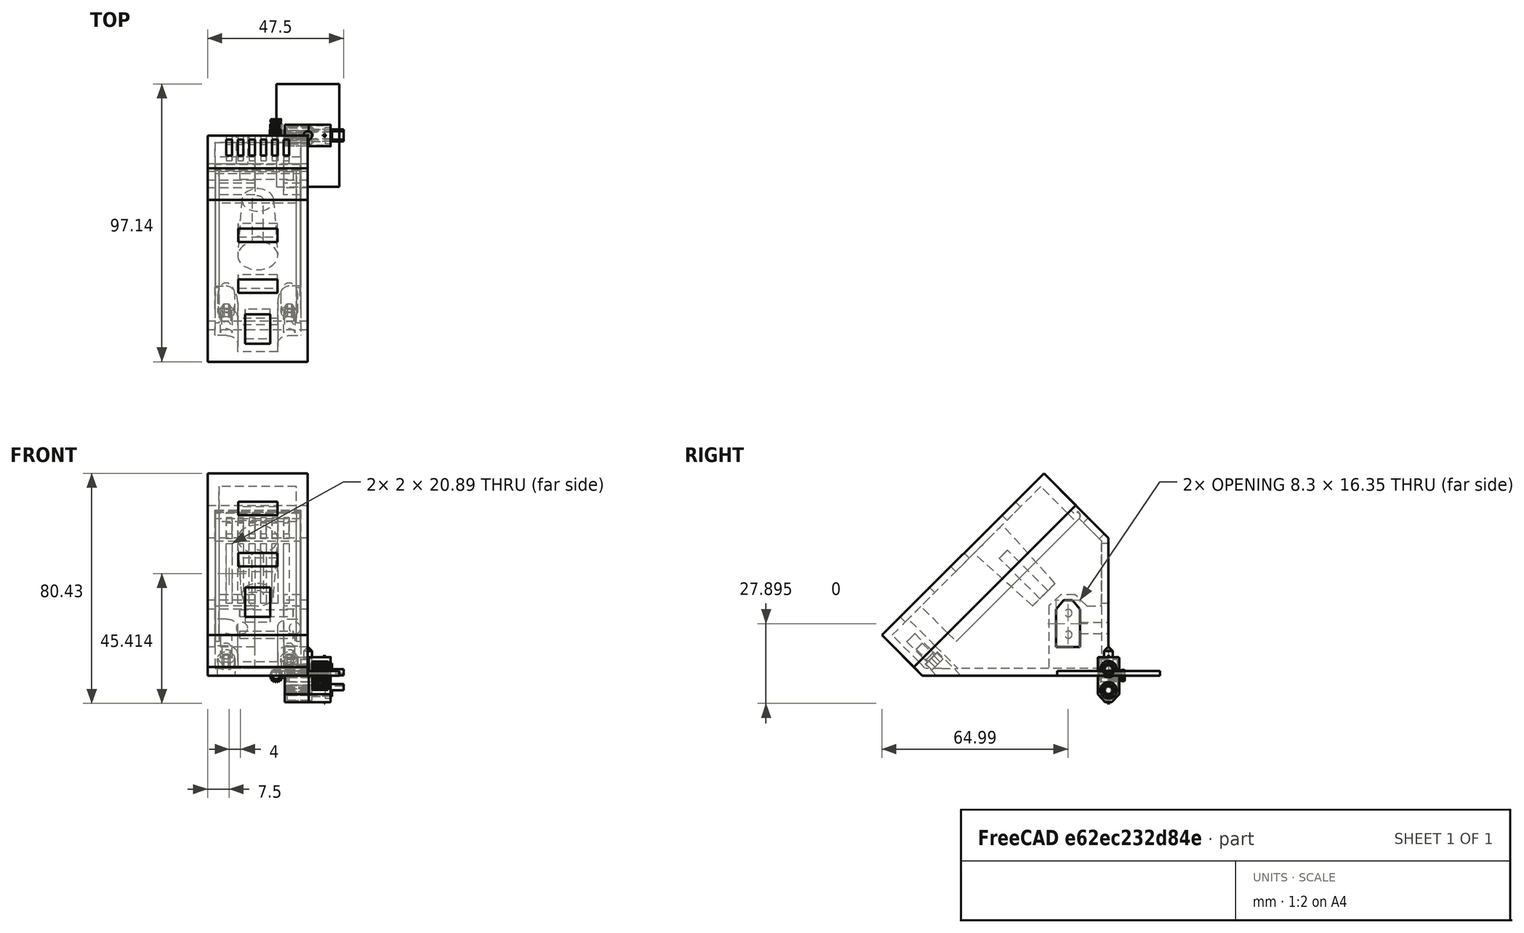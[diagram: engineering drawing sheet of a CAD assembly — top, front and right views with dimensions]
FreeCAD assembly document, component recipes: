
FREECAD ASSEMBLY — COMPONENT RECIPES ("moduleUSB_IP6505_QC2Sur_base35mm_012")

This assembly document has 12 components, labeled P0..P11 below (a component is one placed body or linked part). 10 of them carry a construction recipe — the FreeCAD feature program that regenerates the part from scratch, quoted from this document or its linked companion documents; the rest are supplied as boundary geometry only. No exploded tour is included for this assembly.
COMPONENT P0 — recipe-attached ("base", modeled in this document).
Construction recipe (the document's own serialized feature program — sketch geometry with constraints, then the solid features built on it; lengths are millimeters unless a unit is written):

FEATURE [PartDesign::FeatureBase] Clone
  BaseFeature = -> Slice_child0
FEATURE [PartDesign::Thickness] Thickness
  Base = -> Clone [Face7]
  BaseFeature = -> Clone
  Intersection = false
  Join = 0
  Mode = 0
  Reversed = true
  SupportTransform = false
  Value = 2.5
  expr: Value = <<sp>>.epaisseurParois
FEATURE [PartDesign::Plane] DatumPlane001  label="planXt"
  AttachmentOffset = pos=(0,0,-2.5) rot=(0,0,1;0rad)
  Length = 110.737
  MapMode = 5
  Placement = pos=(-2.5,6e-16,-6e-16) rot=(0.57735,0.57735,0.57735;2.0944rad)
  ResizeMode = 0
  Support = -> [YZ_Plane002]
  Width = 102.305
  expr: .AttachmentOffset.Base.z = -<<sp>>.epaisseurParois
FEATURE [Sketcher::SketchObject] Sketch002  label="sk_renfortXt"
  FullyConstrained = true
  MapMode = 5
  Placement = pos=(-2.5,6e-16,-6e-16) rot=(0.57735,0.57735,0.57735;2.0944rad)
  Support = -> [DatumPlane001]
  expr: .Constraints.dist = <<sp>>.xt60distanceAngleBord
  expr: .Constraints.epRf = <<sp>>.xt60epRenfort
  expr: Constraints[13] = <<sp>>.xt60largeurFetiere
  expr: Constraints[14] = <<sp>>.xt60hauteur
  expr: Constraints[15] = <<sp>>.xt60hauteurToit
  expr: Constraints[16] = <<sp>>.xt60base
  expr: Constraints[18] = .Constraints.dist
  expr: Constraints[31] = <<sp>>.epaisseurParois
  expr: Constraints[32] = .Constraints.epRf
  expr: Constraints[34] = .Constraints.epRf
  expr: Constraints[45] = <<sp>>.epaisseurParois
  sketch-geometry (17):
    g0: LineSegment StartX=-18.3 StartY=10 StartZ=0 EndX=-18.3 EndY=23.25 EndZ=0
    g1: LineSegment StartX=-18.3 StartY=23.25 StartZ=0 EndX=-15.65 EndY=25.75 EndZ=0
    g2: LineSegment StartX=-15.65 StartY=25.75 StartZ=0 EndX=-12.65 EndY=25.75 EndZ=0
    g3: LineSegment StartX=-12.65 StartY=25.75 StartZ=0 EndX=-10 EndY=23.25 EndZ=0
    g4: LineSegment StartX=-10 StartY=23.25 StartZ=0 EndX=-10 EndY=10 EndZ=0
    g5: LineSegment StartX=-10 StartY=10 StartZ=0 EndX=-18.3 EndY=10 EndZ=0
    g6: LineSegment StartX=-14.15 StartY=10 StartZ=0 EndX=-14.15 EndY=25.75 EndZ=0
    g7: LineSegment StartX=-16.6431 StartY=28.25 StartZ=0 EndX=-20.8 EndY=24.3284 EndZ=0
    g8: LineSegment StartX=-20.8 StartY=24.3284 StartZ=0 EndX=-20.8 EndY=2.5 EndZ=0
    g9: LineSegment StartX=-20.8 StartY=2.5 StartZ=0 EndX=-7.5 EndY=2.5 EndZ=0
    g10: LineSegment StartX=-7.5 StartY=2.5 StartZ=0 EndX=-7.5 EndY=24.3284 EndZ=0
    g11: LineSegment StartX=-7.5 StartY=24.3284 StartZ=0 EndX=-11.6569 EndY=28.25 EndZ=0
    g12: LineSegment StartX=-11.6569 StartY=28.25 StartZ=0 EndX=-16.6431 EndY=28.25 EndZ=0
    g13: LineSegment StartX=-7.5 StartY=24.3284 StartZ=0 EndX=-2.5 EndY=24.3284 EndZ=0
    g14: LineSegment StartX=-2.5 StartY=24.3284 StartZ=0 EndX=-2.5 EndY=2.5 EndZ=0
    g15: LineSegment StartX=-2.5 StartY=2.5 StartZ=0 EndX=-7.5 EndY=2.5 EndZ=0
    g16: LineSegment StartX=-7.5 StartY=2.5 StartZ=0 EndX=-7.5 EndY=24.3284 EndZ=0
  constraints (46):
    c: Vertical(g0)
    c: Coincident(g0,g1)
    c: Coincident(g1,g2)
    c: Horizontal(g2)
    c: Coincident(g2,g3)
    c: Coincident(g3,g4)
    c: Vertical(g4)
    c: Coincident(g4,g5)
    c: Coincident(g5,g0)
    c: Horizontal(g5)
    c: Symmetric(g1,g2,g6)
    c: Equal(g0,g4)
    c: Symmetric(g0,g4,g6)
    c: DistanceX(g2,g2) = 3
    c: DistanceY(g4,g4) = 13.25
    c: DistanceY(g3,g2) = 2.5
    c: DistanceX(g5,g5) = 8.3
    c: DistanceX(g4,g-1) = 10  'dist'
    c: DistanceY(g-1,g4) = 10
    c: Coincident(g7,g8)
    c: Vertical(g8)
    c: Coincident(g8,g9)
    c: Horizontal(g9)
    c: Coincident(g9,g10)
    c: Coincident(g10,g11)
    c: Coincident(g11,g12)
    c: Coincident(g12,g7)
    c: Symmetric(g7,g10,g6)
    c: Symmetric(g7,g11,g6)
    c: Symmetric(g8,g9,g6)
    c: DistanceX(g8,g0) = 2.5  'epRf'
    c: DistanceY(g-1,g9) = 2.5
    c: Distance(g7,g1) = 2.5
    c: Parallel(g1,g7)
    c: DistanceY(g2,g11) = 2.5
    c: Coincident(g13,g14)
    c: Coincident(g14,g15)
    c: Coincident(g15,g16)
    c: Coincident(g16,g13)
    c: Horizontal(g13)
    c: Horizontal(g15)
    c: Vertical(g14)
    c: Vertical(g16)
    c: Coincident(g13,g11)
    c: Horizontal(g14,g9)
    c: DistanceX(g14,g-1) = 2.5
FEATURE [PartDesign::Pad] Pad001  label="renfortXt"
  AllowMultiFace = false
  BaseFeature = -> Thickness
  Direction = (1,-1e-16,1e-16)
  Length = 30
  Length2 = 100
  Profile = -> Sketch002
  Reversed = true
  Type = 0
  expr: Length = <<sp>>.largeurModuleBase - 2 * <<sp>>.epaisseurParois
FEATURE [Sketcher::SketchObject] Sketch003  label="sk_trouXt"
  FullyConstrained = true
  MapMode = 5
  Placement = pos=(0,0,0) rot=(0.57735,0.57735,0.57735;2.0944rad)
  Support = -> [YZ_Plane002]
  expr: .Constraints.dist = <<sp>>.xt60distanceAngleBord
  expr: Constraints[13] = <<sp>>.xt60base
  expr: Constraints[14] = <<sp>>.xt60hauteur
  expr: Constraints[15] = <<sp>>.xt60hauteurToit + <<sp>>.xtJeu
  expr: Constraints[16] = <<sp>>.xt60largeurFetiere
  expr: Constraints[18] = .Constraints.dist
  sketch-geometry (7):
    g0: LineSegment StartX=-18.3 StartY=10 StartZ=0 EndX=-18.3 EndY=23.25 EndZ=0
    g1: LineSegment StartX=-18.3 StartY=23.25 StartZ=0 EndX=-15.65 EndY=26.35 EndZ=0
    g2: LineSegment StartX=-15.65 StartY=26.35 StartZ=0 EndX=-12.65 EndY=26.35 EndZ=0
    g3: LineSegment StartX=-12.65 StartY=26.35 StartZ=0 EndX=-10 EndY=23.25 EndZ=0
    g4: LineSegment StartX=-10 StartY=23.25 StartZ=0 EndX=-10 EndY=10 EndZ=0
    g5: LineSegment StartX=-10 StartY=10 StartZ=0 EndX=-18.3 EndY=10 EndZ=0
    g6: LineSegment StartX=-14.15 StartY=10 StartZ=0 EndX=-14.15 EndY=26.35 EndZ=0
  constraints (19):
    c: Vertical(g0)
    c: Coincident(g0,g1)
    c: Coincident(g1,g2)
    c: Horizontal(g2)
    c: Coincident(g2,g3)
    c: Coincident(g3,g4)
    c: Coincident(g4,g5)
    c: Coincident(g5,g0)
    c: Horizontal(g5)
    c: Symmetric(g1,g2,g6)
    c: Symmetric(g0,g3,g6)
    c: Vertical(g6)
    c: Symmetric(g0,g4,g6)
    c: DistanceX(g5,g5) = 8.3
    c: DistanceY(g4,g4) = 13.25
    c: DistanceY(g3,g2) = 3.1
    c: DistanceX(g2,g2) = 3
    c: DistanceX(g4,g-1) = 10  'dist'
    c: DistanceY(g-1,g4) = 10
FEATURE [PartDesign::Pocket] Pocket
  AllowMultiFace = false
  BaseFeature = -> Pad001
  Direction = (-1,2e-16,-3e-16)
  Length = 35
  Length2 = 100
  Profile = -> Sketch003
  Type = 0
  expr: Length = <<sp>>.largeurModuleBase
FEATURE [PartDesign::Plane] DatumPlane002  label="planDecoupeRenfortXt"
  AttachmentOffset = pos=(0,0,2.5) rot=(0,0,1;0rad)
  Length = 74.2466
  MapMode = 5
  Placement = pos=(0,-2.5,-6e-16) rot=(1,0,0;1.5708rad)
  ResizeMode = 0
  Support = -> [XZ_Plane002]
  Width = 98.8151
  expr: .AttachmentOffset.Base.z = <<sp>>.epaisseurParois
FEATURE [Sketcher::SketchObject] Sketch004  label="sk_decoupRenfXt"
  FullyConstrained = true
  MapMode = 5
  Placement = pos=(0,-2.5,-6e-16) rot=(1,0,0;1.5708rad)
  Support = -> [DatumPlane002]
  expr: Constraints[10] = <<sp>>.xt60LongueurRenfortPetit + <<sp>>.epaisseurParois
  expr: Constraints[11] = <<sp>>.largeurModuleBase - (<<sp>>.xt60longueurRenfortGrand + <<sp>>.epaisseurParois)
  expr: Constraints[8] = <<sp>>.epaisseurParois
  expr: Constraints[9] = <<sp>>.xt60distanceAngleBord + <<sp>>.xt60hauteur + <<sp>>.xt60hauteurToit + <<sp>>.xt60epRenfort
  sketch-geometry (4):
    g0: LineSegment StartX=-18.5 StartY=28.25 StartZ=0 EndX=-8.5 EndY=28.25 EndZ=0
    g1: LineSegment StartX=-8.5 StartY=28.25 StartZ=0 EndX=-8.5 EndY=2.5 EndZ=0
    g2: LineSegment StartX=-8.5 StartY=2.5 StartZ=0 EndX=-18.5 EndY=2.5 EndZ=0
    g3: LineSegment StartX=-18.5 StartY=2.5 StartZ=0 EndX=-18.5 EndY=28.25 EndZ=0
  constraints (12):
    c: Coincident(g0,g1)
    c: Coincident(g1,g2)
    c: Coincident(g2,g3)
    c: Coincident(g3,g0)
    c: Horizontal(g0)
    c: Horizontal(g2)
    c: Vertical(g1)
    c: Vertical(g3)
    c: DistanceY(g-1,g1) = 2.5
    c: DistanceY(g-1,g0) = 28.25
    c: DistanceX(g1,g-1) = 8.5
    c: DistanceX(g2,g-1) = 18.5
FEATURE [PartDesign::Pocket] Pocket001  label="decoupeRenfXt"
  AllowMultiFace = false
  BaseFeature = -> Pocket
  Direction = (0,1,2e-16)
  Length = 23.3
  Length2 = 100
  Profile = -> Sketch004
  Reversed = true
  Type = 0
  expr: Length = <<sp>>.xt60distanceAngleBord + <<sp>>.xt60base + 2 * <<sp>>.xt60epRenfort
FEATURE [Sketcher::SketchObject] Sketch005  label="xt60PercagePostMale"
  FullyConstrained = true
  MapMode = 5
  Placement = pos=(0,0,0) rot=(1,0,0;1.5708rad)
  Support = -> [XZ_Plane002]
  expr: Constraints[0] = <<sp>>.insertDiamPercage
  expr: Constraints[1] = <<sp>>.insertDistanceTrouBordMale
  expr: Constraints[2] = <<sp>>.insertHauteur
  sketch-geometry (1):
    g0: Circle CenterX=-4.5 CenterY=16.625 CenterZ=0 NormalX=0 NormalY=0 NormalZ=1 AngleXU=0 Radius=2
  constraints (3):
    c: Diameter(g0) = 4
    c: DistanceX(g0,g-1) = 4.5
    c: DistanceY(g-1,g0) = 16.625
FEATURE [PartDesign::Pocket] Pocket002  label="insertXtMale"
  AllowMultiFace = false
  BaseFeature = -> Pocket001
  Direction = (0,1,2e-16)
  Length = 10
  Length2 = 100
  Profile = -> Sketch005
  Reversed = true
  Type = 0
  expr: Length = <<sp>>.insertProfondeurPercage
FEATURE [Sketcher::SketchObject] Sketch006  label="xt60PercagePostFem"
  FullyConstrained = true
  MapMode = 5
  Placement = pos=(0,0,0) rot=(1,0,0;1.5708rad)
  Support = -> [XZ_Plane002]
  expr: Constraints[0] = <<sp>>.insertDiamPercage
  expr: Constraints[1] = <<sp>>.insertDistanceTrouBordFem
  expr: Constraints[2] = <<sp>>.insertHauteur
  sketch-geometry (1):
    g0: Circle CenterX=-23 CenterY=16.625 CenterZ=0 NormalX=0 NormalY=0 NormalZ=1 AngleXU=0 Radius=2
  constraints (3):
    c: Diameter(g0) = 4
    c: DistanceX(g0,g-1) = 23
    c: DistanceY(g-1,g0) = 16.625
FEATURE [PartDesign::Pocket] Pocket003  label="insertXt60Fem"
  AllowMultiFace = false
  BaseFeature = -> Pocket002
  Direction = (0,1,2e-16)
  Length = 10
  Length2 = 100
  Profile = -> Sketch006
  Reversed = true
  Type = 0
  expr: Length = <<sp>>.insertProfondeurPercage
FEATURE [PartDesign::Plane] DatumPlane003
  AttachmentOffset = pos=(0,0,2.5) rot=(0,0,1;0rad)
  Length = 74.9399
  MapMode = 2
  Placement = pos=(0,0,2.5) rot=(0,0,1;0rad)
  ResizeMode = 0
  Support = -> [XY_Plane002]
  Width = 107.94
  expr: .AttachmentOffset.Base.z = <<sp>>.epaisseurParois
FEATURE [PartDesign::Plane] DatumPlane004  label="planTrancheur"
  AttachmentOffset = pos=(0,0,71) rot=(-1,0,0;0.785398rad)
  Length = 77.3593
  MapMode = 5
  Placement = pos=(0,-71,-1.58e-14) rot=(1,0,0;0.785398rad)
  ResizeMode = 0
  Support = -> [XZ_Plane002]
  Width = 142.919
  expr: .AttachmentOffset.Base.z = <<sp>>.planTrancheur
FEATURE [Sketcher::SketchObject] Sketch008
  FullyConstrained = true
  MapMode = 5
  Placement = pos=(0,-71,-2.13e-14) rot=(1,0,0;0.785398rad)
  Support = -> [DatumPlane004]
  expr: .Constraints.dist = <<sp>>.epaisseurParois
  expr: Constraints[13] = <<sp>>.epaisseurParois
  expr: Constraints[16] = <<sp>>.insertDiamPercage / 2 + <<sp>>.insertFAVMargeDist
  expr: Constraints[1] = <<sp>>.insertFavDistAuZeroDuPLan
  expr: Constraints[21] = <<sp>>.insertFAVDistBord
  expr: Constraints[22] = <<sp>>.largeurModuleBase - <<sp>>.epaisseurParois
  sketch-geometry (7):
    g0: LineSegment StartX=-2.5 StartY=4.24264 StartZ=0 EndX=-32.5 EndY=4.24264 EndZ=0
    g1: LineSegment StartX=-6.5 StartY=14.7426 StartZ=0 EndX=-2.5 EndY=14.7426 EndZ=0
    g2: LineSegment StartX=-2.5 StartY=14.7426 StartZ=0 EndX=-2.5 EndY=6.74264 EndZ=0
    g3: LineSegment StartX=-2.5 StartY=6.74264 StartZ=0 EndX=-10.5 EndY=6.74264 EndZ=0
    g4: LineSegment StartX=-10.5 StartY=6.74264 StartZ=0 EndX=-10.5 EndY=10.7426 EndZ=0
    g5: ArcOfCircle CenterX=-6.5 CenterY=10.7426 CenterZ=0 NormalX=0 NormalY=0 NormalZ=1 AngleXU=0 Radius=4 StartAngle=1.5708 EndAngle=3.14159
    g6: LineSegment StartX=-6.5 StartY=10.7426 StartZ=0 EndX=-6.5 EndY=6.74264 EndZ=0
  constraints (23):
    c: Horizontal(g0)
    c: DistanceY(g-1,g0) = 4.24264
    c: DistanceX(g0,g-1) = 2.5  'dist'
    c: Horizontal(g1)
    c: Coincident(g1,g2)
    c: Vertical(g2)
    c: Coincident(g2,g3)
    c: Horizontal(g3)
    c: Coincident(g3,g4)
    c: Vertical(g4)
    c: Vertical(g2,g0)
    c: Equal(g3,g2)
    c: Equal(g4,g1)
    c: DistanceY(g0,g2) = 2.5
    c: Coincident(g5,g4)
    c: Coincident(g5,g1)
    c: DistanceX(g5,g2) = 4
    c: Coincident(g6,g5)
    c: PointOnObject(g6,g3)
    c: Vertical(g6)
    c: Vertical(g5,g1)
    c: DistanceX(g3,g3) = 8
    c: DistanceX(g0,g-1) = 32.5
FEATURE [PartDesign::Pad] Pad003  label="padTrouFAVDroite"
  AllowMultiFace = false
  BaseFeature = -> Pocket003
  Direction = (0,-0.707107,0.707107)
  Length = 10
  Length2 = 100
  Profile = -> Sketch008
  Reversed = true
  Type = 3
  UpToFace = -> DatumPlane003
FEATURE [Sketcher::SketchObject] Sketch009
  FullyConstrained = true
  MapMode = 5
  Placement = pos=(0,-71,-2.13e-14) rot=(1,0,0;0.785398rad)
  Support = -> [DatumPlane004]
  expr: .Constraints.larg = <<sp>>.insertFAVDistBord
  expr: Constraints[11] = .Constraints.larg / 2
  expr: Constraints[12] = <<sp>>.largeurModuleBase
  expr: Constraints[13] = <<sp>>.insertFavDistAuZeroDuPLan
  expr: Constraints[14] = <<sp>>.epaisseurParois
  expr: Constraints[15] = <<sp>>.epaisseurParois
  expr: Constraints[8] = .Constraints.larg
  sketch-geometry (6):
    g0: LineSegment StartX=-32.5 StartY=6.74264 StartZ=0 EndX=-24.5 EndY=6.74264 EndZ=0
    g1: LineSegment StartX=-24.5 StartY=6.74264 StartZ=0 EndX=-24.5 EndY=10.7426 EndZ=0
    g2: LineSegment StartX=-28.5 StartY=14.7426 StartZ=0 EndX=-32.5 EndY=14.7426 EndZ=0
    g3: LineSegment StartX=-32.5 StartY=14.7426 StartZ=0 EndX=-32.5 EndY=6.74264 EndZ=0
    g4: ArcOfCircle CenterX=-28.5 CenterY=10.7426 CenterZ=0 NormalX=0 NormalY=0 NormalZ=1 AngleXU=0 Radius=4 StartAngle=2e-16 EndAngle=1.5708
    g5: GeomPoint X=-35 Y=4.24264 Z=0
  constraints (16):
    c: Coincident(g0,g1)
    c: Coincident(g2,g3)
    c: Coincident(g3,g0)
    c: Horizontal(g0)
    c: Horizontal(g2)
    c: Vertical(g1)
    c: Vertical(g3)
    c: DistanceX(g0,g0) = 8  'larg'
    c: DistanceY(g3,g3) = 8
    c: Tangent(g2,g4) = -1.5708
    c: Tangent(g1,g4) = -1.5708
    c: DistanceX(g0,g4) = 4
    c: DistanceX(g5,g-1) = 35
    c: DistanceY(g-1,g5) = 4.24264
    c: DistanceX(g5,g0) = 2.5
    c: DistanceY(g5,g0) = 2.5
FEATURE [PartDesign::Pad] Pad004  label="padTrouFavGauche"
  AllowMultiFace = false
  BaseFeature = -> Pad003
  Direction = (0,-0.707107,0.707107)
  Length = 10
  Length2 = 100
  Profile = -> Sketch009
  Type = 3
  UpToFace = -> DatumPlane003 [Plane]
FEATURE [Sketcher::SketchObject] Sketch010
  FullyConstrained = true
  MapMode = 5
  Placement = pos=(0,-71,-2.13e-14) rot=(1,0,0;0.785398rad)
  Support = -> [DatumPlane004]
  expr: Constraints[0] = <<sp>>.insertFAVDistBord / 2 + <<sp>>.epaisseurParois
  expr: Constraints[1] = <<sp>>.insertFavDistAuZeroDuPLan + <<sp>>.epaisseurParois + <<sp>>.insertFAVDistBord / 2
  expr: Constraints[2] = <<sp>>.insertDiamPercage
  sketch-geometry (1):
    g0: Circle CenterX=-6.5 CenterY=10.7426 CenterZ=0 NormalX=0 NormalY=0 NormalZ=1 AngleXU=0 Radius=2
  constraints (3):
    c: DistanceX(g0,g-1) = 6.5
    c: DistanceY(g-1,g0) = 10.7426
    c: Diameter(g0) = 4
FEATURE [PartDesign::Pocket] Pocket004  label="trouDroit"
  AllowMultiFace = false
  BaseFeature = -> Pad004
  Direction = (0,0.707107,-0.707107)
  Length = 5
  Length2 = 100
  Profile = -> Sketch010
  Type = 1
FEATURE [Sketcher::SketchObject] Sketch011
  FullyConstrained = true
  MapMode = 5
  Placement = pos=(0,-71,-2.13e-14) rot=(1,0,0;0.785398rad)
  Support = -> [DatumPlane004]
  expr: Constraints[0] = <<sp>>.insertDiamPercage
  expr: Constraints[1] = <<sp>>.largeurModuleBase - <<sp>>.epaisseurParois - <<sp>>.insertFAVDistBord / 2
  expr: Constraints[2] = <<sp>>.insertFavDistAuZeroDuPLan + <<sp>>.epaisseurParois + <<sp>>.insertFAVDistBord / 2
  sketch-geometry (1):
    g0: Circle CenterX=-28.5 CenterY=10.7426 CenterZ=0 NormalX=0 NormalY=0 NormalZ=1 AngleXU=0 Radius=2
  constraints (3):
    c: Diameter(g0) = 4
    c: DistanceX(g0,g-1) = 28.5
    c: DistanceY(g-1,g0) = 10.7426
FEATURE [PartDesign::Pocket] Pocket005  label="trouGauche"
  AllowMultiFace = false
  BaseFeature = -> Pocket004
  Direction = (0,0.707107,-0.707107)
  Length = 5
  Length2 = 100
  Profile = -> Sketch011
  Type = 1
FEATURE [PartDesign::Plane] DatumPlane005  label="planTeteVisFav"
  AttachmentOffset = pos=(0,0,68) rot=(-1,0,0;0.785398rad)
  Length = 77.3593
  MapMode = 5
  Placement = pos=(0,-68,-1.51e-14) rot=(1,0,0;0.785398rad)
  ResizeMode = 0
  Support = -> [XZ_Plane002]
  Width = 142.919
  expr: .AttachmentOffset.Base.z = <<sp>>.planTrancheur - 3
FEATURE [Sketcher::SketchObject] Sketch012
  ExternalGeometry = -> [Pocket005]
  FullyConstrained = true
  MapMode = 5
  Placement = pos=(0,-68,-1.42e-14) rot=(1,0,0;0.785398rad)
  Support = -> [DatumPlane005]
  expr: Constraints[1] = <<sp>>.visM3DiamEncastrement
  sketch-geometry (2):
    g0: Circle CenterX=-6.5 CenterY=8.62132 CenterZ=0 NormalX=0 NormalY=0 NormalZ=1 AngleXU=0 Radius=3
    g1: Circle CenterX=-28.5 CenterY=8.62132 CenterZ=0 NormalX=0 NormalY=0 NormalZ=1 AngleXU=0 Radius=3
  constraints (4):
    c: Equal(g0,g1)
    c: Diameter(g1) = 6
    c: Coincident(g1,g-4)
    c: Coincident(g-3,g0)
FEATURE [PartDesign::Pocket] Pocket006  label="evidementTeteVisFav"
  AllowMultiFace = false
  BaseFeature = -> Pocket005
  Direction = (0,0.707107,-0.707107)
  Length = 20
  Length2 = 100
  Profile = -> Sketch012
  Type = 1
FEATURE [Sketcher::SketchObject] Sketch014
  FullyConstrained = true
  MapMode = 5
  Placement = pos=(0,0,0) rot=(1,0,0;1.5708rad)
  Support = -> [XZ_Plane002]
  expr: Constraints[12] = <<sp>>.xt60distanceAngleBord + <<sp>>.xt60hauteur + <<sp>>.ventilDistBordFente
  expr: Constraints[13] = <<sp>>.ventilLargeurFentes
  expr: Constraints[14] = <<sp>>.ventilEcartfente / 2
  expr: Constraints[15] = <<sp>>.hauteurDuDos - <<sp>>.ventilDistBordFente
  expr: Constraints[2] = <<sp>>.hauteurDuDos
  expr: Constraints[3] = <<sp>>.largeurModuleBase / 2
  sketch-geometry (5):
    g0: LineSegment StartX=-17.5 StartY=0 StartZ=0 EndX=-17.5 EndY=48.1371 EndZ=0
    g1: LineSegment StartX=-20.5 StartY=46.1371 StartZ=0 EndX=-18.5 EndY=46.1371 EndZ=0
    g2: LineSegment StartX=-18.5 StartY=46.1371 StartZ=0 EndX=-18.5 EndY=25.25 EndZ=0
    g3: LineSegment StartX=-18.5 StartY=25.25 StartZ=0 EndX=-20.5 EndY=25.25 EndZ=0
    g4: LineSegment StartX=-20.5 StartY=25.25 StartZ=0 EndX=-20.5 EndY=46.1371 EndZ=0
  constraints (16):
    c: PointOnObject(g0,g-1)
    c: Vertical(g0)
    c: DistanceY(g0,g0) = 48.1371
    c: DistanceX(g0,g-1) = 17.5
    c: Coincident(g1,g2)
    c: Coincident(g2,g3)
    c: Coincident(g3,g4)
    c: Coincident(g4,g1)
    c: Horizontal(g1)
    c: Horizontal(g3)
    c: Vertical(g2)
    c: Vertical(g4)
    c: DistanceY(g-1,g2) = 25.25
    c: DistanceX(g1,g1) = 2
    c: DistanceX(g2,g0) = 1
    c: DistanceY(g-1,g1) = 46.1371
FEATURE [PartDesign::Pocket] Pocket008  label="ventilFente1"
  AllowMultiFace = false
  BaseFeature = -> Pocket006
  Direction = (0,1,2e-16)
  Length = 2.5
  Length2 = 100
  Profile = -> Sketch014
  Reversed = true
  Type = 0
  expr: Length = <<sp>>.epaisseurParois
FEATURE [PartDesign::LinearPattern] LinearPattern  label="ventilDosRepeat1"
  BaseFeature = -> Pocket008
  Direction = -> Sketch014 [H_Axis]
  Length = 8
  Occurrences = 3
  Originals = -> [Pocket008]
  Reversed = true
  expr: Length = <<sp>>.ventilLargeurRepet
  expr: Occurrences = <<sp>>.ventilNbrFents
FEATURE [PartDesign::LinearPattern] LinearPattern001  label="ventilDosRepeat2"
  BaseFeature = -> LinearPattern
  Direction = -> Sketch014 [H_Axis]
  Length = 12
  Occurrences = 4
  Originals = -> [Pocket008]
  expr: Length = <<sp>>.ventilLargeurRepet + <<sp>>.ventilEcartfente + <<sp>>.ventilLargeurFentes
  expr: Occurrences = <<sp>>.ventilNbrFents + 1
FEATURE [PartDesign::Plane] DatumPlane006  label="planVentilSup"
  AttachmentOffset = pos=(0,0,-48.1371) rot=(1,0,0;0.785398rad)
  Length = 77.3593
  MapMode = 5
  Placement = pos=(0,48.1371,1.07e-14) rot=(1,0,0;2.35619rad)
  ResizeMode = 0
  Support = -> [XZ_Plane002]
  Width = 142.919
  expr: .AttachmentOffset.Base.z = -<<sp>>.hauteurDuDos
FEATURE [Sketcher::SketchObject] Sketch015
  FullyConstrained = true
  MapMode = 5
  Placement = pos=(0,48.1371,1.07e-14) rot=(1,0,0;2.35619rad)
  Support = -> [DatumPlane006]
  expr: Constraints[10] = <<sp>>.ventilLargeurFentes
  expr: Constraints[11] = (<<sp>>.largeurModuleBase + <<sp>>.ventilEcartfente) / 2
  expr: Constraints[8] = <<sp>>.distanceAuZeroPlanBorArriere + <<sp>>.ventilDistBordFente
  expr: Constraints[9] = <<sp>>.longPetitRetSupSansFav - 2 * <<sp>>.ventilDistBordFente - <<sp>>.favBordureProf
  sketch-geometry (4):
    g0: LineSegment StartX=-18.5 StartY=78.0926 StartZ=0 EndX=-20.5 EndY=78.0926 EndZ=0
    g1: LineSegment StartX=-20.5 StartY=78.0926 StartZ=0 EndX=-20.5 EndY=70.0761 EndZ=0
    g2: LineSegment StartX=-20.5 StartY=70.0761 StartZ=0 EndX=-18.5 EndY=70.0761 EndZ=0
    g3: LineSegment StartX=-18.5 StartY=70.0761 StartZ=0 EndX=-18.5 EndY=78.0926 EndZ=0
  constraints (12):
    c: Coincident(g0,g1)
    c: Coincident(g1,g2)
    c: Coincident(g2,g3)
    c: Coincident(g3,g0)
    c: Horizontal(g0)
    c: Horizontal(g2)
    c: Vertical(g1)
    c: Vertical(g3)
    c: DistanceY(g-1,g2) = 70.0761
    c: DistanceY(g2,g0) = 8.01652
    c: DistanceX(g0,g0) = 2
    c: DistanceX(g2,g-1) = 18.5
FEATURE [PartDesign::Pocket] Pocket009  label="ventilSupFente"
  AllowMultiFace = false
  BaseFeature = -> LinearPattern001
  Direction = (0,0.707107,0.707107)
  Length = 5
  Length2 = 100
  Profile = -> Sketch015
  Reversed = true
  Type = 0
FEATURE [PartDesign::LinearPattern] LinearPattern002  label="ventilSupRepeat1"
  BaseFeature = -> Pocket009
  Direction = -> Sketch015 [H_Axis]
  Length = 8
  Occurrences = 3
  Originals = -> [Pocket009]
  Reversed = true
  expr: Length = <<sp>>.ventilLargeurRepet
  expr: Occurrences = <<sp>>.ventilNbrFents
FEATURE [PartDesign::LinearPattern] LinearPattern003  label="ventilSupRepeat2"
  BaseFeature = -> LinearPattern002
  Direction = -> Sketch015 [H_Axis]
  Length = 12
  Occurrences = 4
  Originals = -> [Pocket009]
  expr: Length = <<sp>>.ventilLargeurRepet + <<sp>>.ventilEcartfente + <<sp>>.ventilLargeurFentes
  expr: Occurrences = <<sp>>.ventilNbrFents + 1
FEATURE [PartDesign::Body] Body001  label="base"
  BaseFeature = -> Slice_child0
  Group = -> [Clone,Thickness,DatumPlane001,Sketch002,Pad001,Sketch003,Pocket,DatumPlane002,Sketch004,Pocket001,Sketch005,Pocket002,Sketch006,Pocket003,DatumPlane003,DatumPlane004,Sketch008,Pad003,Sketch009,Pad004,Sketch010,Pocket004,Sketch011,Pocket005,DatumPlane005,Sketch012,Pocket006,Sketch014,Pocket008,LinearPattern,LinearPattern001,DatumPlane006,Sketch015,Pocket009,LinearPattern002,LinearPattern003,+3 more]
  Origin = -> Origin002
  Tip = -> Pocket015
COMPONENT P1 — recipe-attached ("faceAvant", modeled in this document).
Construction recipe (the document's own serialized feature program — sketch geometry with constraints, then the solid features built on it; lengths are millimeters unless a unit is written):

FEATURE [PartDesign::FeatureBase] Clone001
  BaseFeature = -> Slice_child1
FEATURE [PartDesign::Thickness] Thickness001
  Base = -> Clone001 [Face5]
  BaseFeature = -> Clone001
  Intersection = false
  Join = 0
  Mode = 0
  Reversed = true
  SupportTransform = false
  Value = 2.5
  expr: Value = <<sp>>.epaisseurParois
FEATURE [PartDesign::Plane] DatumPlane007  label="planTrancheurBis"
  AttachmentOffset = pos=(0,0,71) rot=(-1,0,0;0.785398rad)
  Length = 78.4163
  MapMode = 5
  Placement = pos=(0,-71,-1.58e-14) rot=(1,0,0;0.785398rad)
  ResizeMode = 0
  Support = -> [XZ_Plane003]
  Width = 159.734
  expr: .AttachmentOffset.Base.z = <<sp>>.planTrancheur
FEATURE [Sketcher::SketchObject] Sketch016  label="sk_insertFavDroit"
  FullyConstrained = true
  MapMode = 5
  Placement = pos=(0,-71,-2.13e-14) rot=(1,0,0;0.785398rad)
  Support = -> [DatumPlane007]
  expr: Constraints[11] = <<sp>>.insertFAVDistBord
  expr: Constraints[14] = <<sp>>.insertFAVDistBord / 2
  expr: Constraints[7] = <<sp>>.epaisseurParois
  expr: Constraints[8] = <<sp>>.insertFavDistAuZeroDuPLan + <<sp>>.epaisseurParois
  expr: Constraints[9] = <<sp>>.insertFAVDistBord
  sketch-geometry (5):
    g0: LineSegment StartX=-6.5 StartY=14.7426 StartZ=0 EndX=-2.5 EndY=14.7426 EndZ=0
    g1: LineSegment StartX=-2.5 StartY=14.7426 StartZ=0 EndX=-2.5 EndY=6.74264 EndZ=0
    g2: LineSegment StartX=-2.5 StartY=6.74264 StartZ=0 EndX=-10.5 EndY=6.74264 EndZ=0
    g3: LineSegment StartX=-10.5 StartY=6.74264 StartZ=0 EndX=-10.5 EndY=10.7426 EndZ=0
    g4: ArcOfCircle CenterX=-6.5 CenterY=10.7426 CenterZ=0 NormalX=0 NormalY=0 NormalZ=1 AngleXU=0 Radius=4 StartAngle=1.5708 EndAngle=3.14159
  constraints (15):
    c: Horizontal(g0)
    c: Coincident(g0,g1)
    c: Vertical(g1)
    c: Coincident(g1,g2)
    c: Horizontal(g2)
    c: Coincident(g2,g3)
    c: Vertical(g3)
    c: DistanceX(g1,g-1) = 2.5
    c: DistanceY(g-1,g1) = 6.74264
    c: DistanceY(g1,g1) = 8
    c: Equal(g3,g0)
    c: DistanceX(g2,g2) = 8
    c: Coincident(g4,g0)
    c: Tangent(g4,g3) = 1.5708
    c: DistanceX(g4,g1) = 4
FEATURE [PartDesign::Pad] Pad005  label="padInsertFavDroit"
  AllowMultiFace = false
  BaseFeature = -> Thickness001
  Direction = (0,-0.707107,0.707107)
  Length = 10
  Length2 = 100
  Profile = -> Sketch016
  Type = 2
FEATURE [Sketcher::SketchObject] Sketch017  label="sp_padInserFavGauch"
  FullyConstrained = true
  MapMode = 5
  Placement = pos=(0,-71,-2.13e-14) rot=(1,0,0;0.785398rad)
  Support = -> [DatumPlane007]
  expr: Constraints[10] = <<sp>>.insertFAVDistBord
  expr: Constraints[12] = <<sp>>.insertFAVDistBord / 2
  expr: Constraints[13] = <<sp>>.largeurModuleBase
  expr: Constraints[14] = <<sp>>.insertFavDistAuZeroDuPLan
  expr: Constraints[15] = <<sp>>.epaisseurParois
  expr: Constraints[16] = <<sp>>.epaisseurParois
  sketch-geometry (6):
    g0: LineSegment StartX=-28.5 StartY=14.7426 StartZ=0 EndX=-32.5 EndY=14.7426 EndZ=0
    g1: LineSegment StartX=-32.5 StartY=14.7426 StartZ=0 EndX=-32.5 EndY=6.74264 EndZ=0
    g2: LineSegment StartX=-32.5 StartY=6.74264 StartZ=0 EndX=-24.5 EndY=6.74264 EndZ=0
    g3: LineSegment StartX=-24.5 StartY=6.74264 StartZ=0 EndX=-24.5 EndY=10.7426 EndZ=0
    g4: ArcOfCircle CenterX=-28.5 CenterY=10.7426 CenterZ=0 NormalX=0 NormalY=0 NormalZ=1 AngleXU=0 Radius=4 StartAngle=-1.32614e-11 EndAngle=1.5708
    g5: GeomPoint X=-35 Y=4.24264 Z=0
  constraints (17):
    c: Horizontal(g0)
    c: Coincident(g0,g1)
    c: Vertical(g1)
    c: Coincident(g1,g2)
    c: Horizontal(g2)
    c: Coincident(g2,g3)
    c: Vertical(g3)
    c: Equal(g3,g0)
    c: Equal(g2,g1)
    c: Coincident(g0,g4)
    c: DistanceX(g2,g2) = 8
    c: Tangent(g4,g3) = -1.5708
    c: DistanceX(g0,g0) = 4
    c: DistanceX(g5,g-1) = 35
    c: DistanceY(g-1,g5) = 4.24264
    c: DistanceY(g5,g1) = 2.5
    c: DistanceX(g5,g1) = 2.5
FEATURE [PartDesign::Pad] Pad006  label="padInsertFavGauch"
  AllowMultiFace = false
  BaseFeature = -> Pad005
  Direction = (0,-0.707107,0.707107)
  Length = 10
  Length2 = 100
  Profile = -> Sketch017
  Type = 2
FEATURE [Sketcher::SketchObject] Sketch018  label="skPercageInsertFavDroit"
  FullyConstrained = true
  MapMode = 5
  Placement = pos=(0,-71,-2.13e-14) rot=(1,0,0;0.785398rad)
  Support = -> [DatumPlane007]
  expr: Constraints[0] = <<sp>>.insertDiamPercage
  expr: Constraints[1] = <<sp>>.insertFavDistAuZeroDuPLan + <<sp>>.epaisseurParois + <<sp>>.insertFAVDistBord / 2
  expr: Constraints[2] = <<sp>>.epaisseurParois + <<sp>>.insertFAVDistBord / 2
  expr: Constraints[7] = <<sp>>.largeurModuleBase - 2 * <<sp>>.epaisseurParois - <<sp>>.insertFAVDistBord
  sketch-geometry (3):
    g0: Circle CenterX=-6.5 CenterY=10.7426 CenterZ=0 NormalX=0 NormalY=0 NormalZ=1 AngleXU=0 Radius=2
    g1: Circle CenterX=-28.5 CenterY=10.7426 CenterZ=0 NormalX=0 NormalY=0 NormalZ=1 AngleXU=0 Radius=2
    g2: LineSegment StartX=-28.5 StartY=10.7426 StartZ=0 EndX=-6.5 EndY=10.7426 EndZ=0
  constraints (8):
    c: Diameter(g0) = 4
    c: DistanceY(g-1,g0) = 10.7426
    c: DistanceX(g0,g-1) = 6.5
    c: Equal(g0,g1)
    c: Coincident(g2,g1)
    c: Coincident(g2,g0)
    c: Horizontal(g2)
    c: DistanceX(g2,g2) = 22
FEATURE [PartDesign::Pocket] Pocket010  label="trouInsertFavDroit"
  AllowMultiFace = false
  BaseFeature = -> Pad006
  Direction = (0,0.707107,-0.707107)
  Length = 8
  Length2 = 100
  Profile = -> Sketch018
  Reversed = true
  Type = 0
  expr: Length = <<sp>>.insertFavProfondeur
FEATURE [PartDesign::Plane] DatumPlane011  label="planFaceAvant"
  AttachmentOffset = pos=(0,0,93.2843) rot=(-1,0,0;0.785398rad)
  Length = 78.4163
  MapMode = 5
  Placement = pos=(0,-93.2843,-2.07e-14) rot=(1,0,0;0.785398rad)
  ResizeMode = 0
  Support = -> [XZ_Plane003]
  Width = 159.734
  expr: .AttachmentOffset.Base.z = <<sp>>.planFaceAvant
FEATURE [Sketcher::SketchObject] Sketch030  label="sk_rebordFav"
  FullyConstrained = true
  MapMode = 5
  Placement = pos=(0,-71,-2.13e-14) rot=(1,0,0;0.785398rad)
  Support = -> [DatumPlane007]
  expr: Constraints[0] = <<sp>>.insertFavDistAuZeroDuPLan
  expr: Constraints[19] = <<sp>>.epaisseurParois
  expr: Constraints[20] = <<sp>>.favEpBordure
  expr: Constraints[21] = <<sp>>.favDistBordPlan
  expr: Constraints[22] = <<sp>>.largeurModuleBase - 2 * <<sp>>.epaisseurParois
  expr: Constraints[23] = <<sp>>.favEpBordure
  expr: Constraints[24] = <<sp>>.Face - <<sp>>.epaisseurParois
  expr: Constraints[25] = <<sp>>.favEpBordure
  sketch-geometry (9):
    g0: GeomPoint X=0 Y=4.24264 Z=0
    g1: LineSegment StartX=-32.5 StartY=20.9853 StartZ=0 EndX=-32.5 EndY=81.7426 EndZ=0
    g2: LineSegment StartX=-32.5 StartY=81.7426 StartZ=0 EndX=-2.5 EndY=81.7426 EndZ=0
    g3: LineSegment StartX=-2.5 StartY=81.7426 StartZ=0 EndX=-2.5 EndY=20.9853 EndZ=0
    g4: LineSegment StartX=-2.5 StartY=20.9853 StartZ=0 EndX=-4 EndY=20.9853 EndZ=0
    g5: LineSegment StartX=-4 StartY=20.9853 StartZ=0 EndX=-4 EndY=80.2426 EndZ=0
    g6: LineSegment StartX=-4 StartY=80.2426 StartZ=0 EndX=-31 EndY=80.2426 EndZ=0
    g7: LineSegment StartX=-31 StartY=80.2426 StartZ=0 EndX=-31 EndY=20.9853 EndZ=0
    g8: LineSegment StartX=-31 StartY=20.9853 StartZ=0 EndX=-32.5 EndY=20.9853 EndZ=0
  constraints (26):
    c: DistanceY(g-1,g0) = 4.24264
    c: Vertical(g0,g-1)
    c: Vertical(g1)
    c: Coincident(g1,g2)
    c: Horizontal(g2)
    c: Coincident(g2,g3)
    c: Vertical(g3)
    c: Coincident(g3,g4)
    c: Horizontal(g4)
    c: Coincident(g4,g5)
    c: Vertical(g5)
    c: Coincident(g5,g6)
    c: Horizontal(g6)
    c: Coincident(g6,g7)
    c: Vertical(g7)
    c: Coincident(g7,g8)
    c: Coincident(g8,g1)
    c: Horizontal(g8)
    c: Horizontal(g7,g4)
    c: DistanceX(g3,g0) = 2.5
    c: DistanceX(g4,g4) = 1.5
    c: DistanceY(g0,g3) = 16.7426
    c: DistanceX(g1,g3) = 30
    c: DistanceY(g5,g2) = 1.5
    c: DistanceY(g0,g2) = 77.5
    c: DistanceX(g1,g7) = 1.5
FEATURE [PartDesign::Pad] Pad014  label="favRebordSupport"
  AllowMultiFace = false
  BaseFeature = -> Pocket010
  Direction = (0,-0.707107,0.707107)
  Length = 10
  Length2 = 100
  Profile = -> Sketch030
  Type = 3
  UpToFace = -> Pocket010 [Face13]
FEATURE [PartDesign::Pad] Pad015  label="favRebord"
  AllowMultiFace = false
  BaseFeature = -> Pad014
  Direction = (0,-0.707107,0.707107)
  Length = 4.15
  Length2 = 100
  Profile = -> Sketch030
  Reversed = true
  Type = 0
  expr: Length = <<sp>>.favBordureProf
FEATURE [Sketcher::SketchObject] Sketch031  label="sk_bourlet"
  ExternalGeometry = -> [Pad015]
  FullyConstrained = true
  MapMode = 5
  Placement = pos=(-2.5,0,0) rot=(0.57735,0.57735,0.57735;2.0944rad)
  Support = -> [Pad015]
  expr: Constraints[3] = <<sp>>.bourletMaintientRayon - <<sp>>.bourletRayonJeu
  sketch-geometry (2):
    g0: ArcOfCircle CenterX=-11.184 CenterY=55.7855 CenterZ=0 NormalX=0 NormalY=0 NormalZ=1 AngleXU=0 Radius=1.3 StartAngle=5.49779 EndAngle=8.63938
    g1: LineSegment StartX=-12.1032 StartY=56.7048 StartZ=0 EndX=-10.2647 EndY=54.8663 EndZ=0
  constraints (6):
    c: Coincident(g0,g-3)
    c: PointOnObject(g0,g-3)
    c: PointOnObject(g0,g-3)
    c: Radius(g0) = 1.3
    c: Coincident(g1,g0)
    c: Coincident(g1,g0)
FEATURE [PartDesign::Pad] Pad016  label="bourlet"
  AllowMultiFace = false
  BaseFeature = -> Pad015
  Direction = (1,0,0)
  Length = 10
  Length2 = 100
  Profile = -> Sketch031
  Reversed = true
  Type = 3
  UpToFace = -> Pad015 [Face11]
FEATURE [Sketcher::SketchObject] Sketch039
  FullyConstrained = true
  MapMode = 5
  Placement = pos=(0,-71,-2.13e-14) rot=(1,0,0;0.785398rad)
  Support = -> [DatumPlane007]
  expr: Constraints[20] = <<sp>>.favBordureJeu / 2
  expr: Constraints[21] = <<sp>>.epaisseurParois
  expr: Constraints[22] = <<sp>>.largeurModuleBase - 2 * <<sp>>.epaisseurParois
  expr: Constraints[23] = <<sp>>.insertFavDistAuZeroDuPLan + <<sp>>.favDistBordPlan
  expr: Constraints[27] = <<sp>>.insertFavDistAuZeroDuPLan + <<sp>>.Face - <<sp>>.epaisseurParois + <<sp>>.bourletMaintientRayon
  sketch-geometry (10):
    g0: LineSegment StartX=-32.5 StartY=83.2426 StartZ=0 EndX=-32.25 EndY=83.2426 EndZ=0
    g1: LineSegment StartX=-32.25 StartY=83.2426 StartZ=0 EndX=-32.25 EndY=20.9853 EndZ=0
    g2: LineSegment StartX=-32.25 StartY=20.9853 StartZ=0 EndX=-32.5 EndY=20.9853 EndZ=0
    g3: LineSegment StartX=-32.5 StartY=20.9853 StartZ=0 EndX=-32.5 EndY=83.2426 EndZ=0
    g4: LineSegment StartX=-2.5 StartY=83.2426 StartZ=0 EndX=-2.75 EndY=83.2426 EndZ=0
    g5: LineSegment StartX=-2.75 StartY=83.2426 StartZ=0 EndX=-2.75 EndY=20.9853 EndZ=0
    g6: LineSegment StartX=-2.75 StartY=20.9853 StartZ=0 EndX=-2.5 EndY=20.9853 EndZ=0
    g7: LineSegment StartX=-2.5 StartY=20.9853 StartZ=0 EndX=-2.5 EndY=83.2426 EndZ=0
    g8: LineSegment StartX=-32.25 StartY=20.9853 StartZ=0 EndX=-2.5 EndY=20.9853 EndZ=0
    g9: LineSegment StartX=-2.75 StartY=83.2426 StartZ=0 EndX=-32.25 EndY=83.2426 EndZ=0
  constraints (28):
    c: Coincident(g0,g1)
    c: Coincident(g1,g2)
    c: Coincident(g2,g3)
    c: Coincident(g3,g0)
    c: Horizontal(g0)
    c: Horizontal(g2)
    c: Vertical(g1)
    c: Vertical(g3)
    c: Coincident(g4,g5)
    c: Coincident(g5,g6)
    c: Coincident(g6,g7)
    c: Coincident(g7,g4)
    c: Horizontal(g4)
    c: Horizontal(g6)
    c: Vertical(g5)
    c: Vertical(g7)
    c: Coincident(g8,g1)
    c: Coincident(g8,g6)
    c: Horizontal(g8)
    c: Equal(g2,g6)
    c: DistanceX(g2,g2) = 0.25
    c: DistanceX(g6,g-1) = 2.5
    c: DistanceX(g2,g6) = 30
    c: DistanceY(g-1,g6) = 20.9853
    c: Coincident(g9,g4)
    c: Coincident(g9,g0)
    c: Horizontal(g9)
    c: DistanceY(g-1,g4) = 83.2426
FEATURE [PartDesign::Pocket] Pocket018  label="ajoutJeuLevreFav"
  BaseFeature = -> Pad016
  Direction = (0,0.707107,-0.707107)
  Length = 4.15
  Length2 = 5
  Profile = -> Sketch039
  ReferenceAxis = -> Sketch039 [N_Axis]
  Type = 0
  expr: Length = <<sp>>.favBordureProf
FEATURE [Sketcher::SketchObject] Sketch042
  AttachmentOffset = pos=(0,0,-2.5) rot=(0,0,1;0rad)
  FullyConstrained = true
  MapMode = 5
  Placement = pos=(0,-91.5165,-1.76777) rot=(1,0,0;0.785398rad)
  Support = -> [DatumPlane011]
  expr: .AttachmentOffset.Base.z = <<sp>>.epaisseurParois * -1
  expr: Constraints[1] = <<sp>>.largeurModuleBase / 2
  expr: Constraints[2] = <<sp>>.distZeroTrouFav
  sketch-geometry (1):
    g0: Circle CenterX=-17.5 CenterY=70 CenterZ=0 NormalX=0 NormalY=0 NormalZ=1 AngleXU=0 Radius=7
  constraints (3):
    c: Diameter(g0) = 14
    c: DistanceX(g0,g-1) = 17.5
    c: DistanceY(g-1,g0) = 70
FEATURE [PartDesign::Pad] Pad024  label="piloneCentral"
  BaseFeature = -> Pocket018
  Direction = (0,-0.707107,0.707107)
  Length = 27.5
  Length2 = 10
  Profile = -> Sketch042
  ReferenceAxis = -> Sketch042 [N_Axis]
  Reversed = true
  TaperAngle = -3
  Type = 0
  expr: Length = <<sp>>.hauteurPilone
FEATURE [Sketcher::SketchObject] Sketch043
  FullyConstrained = true
  MapMode = 5
  Placement = pos=(0,-93.2843,-2.84e-14) rot=(1,0,0;0.785398rad)
  Support = -> [DatumPlane011]
  expr: Constraints[1] = <<sp>>.distZeroPlanFAV
  expr: Constraints[22] = <<sp>>.usblarg + <<sp>>.jeu
  expr: Constraints[24] = <<sp>>.usbhaut
  expr: Constraints[25] = 22.5 + 2.75
  expr: Constraints[28] = 2.75 + 22.5 / 2 + 3 - 1.6 + 0.6
  expr: Constraints[29] = <<sp>>.Face
  expr: Constraints[3] = <<sp>>.largeurModuleBase / 2
  sketch-geometry (13):
    g0: GeomPoint X=0 Y=20 Z=0
    g1: GeomPoint X=-17.5 Y=20 Z=0
    g2: LineSegment StartX=-24.35 StartY=85.89 StartZ=0 EndX=-10.65 EndY=85.89 EndZ=0
    g3: LineSegment StartX=-10.65 StartY=85.89 StartZ=0 EndX=-10.65 EndY=79.25 EndZ=0
    g4: LineSegment StartX=-10.65 StartY=79.25 StartZ=0 EndX=-24.35 EndY=79.25 EndZ=0
    g5: LineSegment StartX=-24.35 StartY=79.25 StartZ=0 EndX=-24.35 EndY=85.89 EndZ=0
    g6: LineSegment StartX=-24.35 StartY=60.64 StartZ=0 EndX=-10.65 EndY=60.64 EndZ=0
    g7: LineSegment StartX=-10.65 StartY=60.64 StartZ=0 EndX=-10.65 EndY=54 EndZ=0
    g8: LineSegment StartX=-10.65 StartY=54 StartZ=0 EndX=-24.35 EndY=54 EndZ=0
    g9: LineSegment StartX=-24.35 StartY=54 StartZ=0 EndX=-24.35 EndY=60.64 EndZ=0
    g10: GeomPoint X=-17.5 Y=70 Z=0
    g11: GeomPoint X=-17.5 Y=100 Z=0
    g12: LineSegment StartX=-17.5 StartY=20 StartZ=0 EndX=-17.5 EndY=100 EndZ=0
  constraints (34):
    c: PointOnObject(g0,g-2)
    c: DistanceY(g-1,g0) = 20
    c: Horizontal(g1,g0)
    c: DistanceX(g1,g0) = 17.5
    c: Coincident(g2,g3)
    c: Coincident(g3,g4)
    c: Coincident(g4,g5)
    c: Coincident(g5,g2)
    c: Horizontal(g2)
    c: Horizontal(g4)
    c: Vertical(g5)
    c: Coincident(g6,g7)
    c: Coincident(g7,g8)
    c: Coincident(g8,g9)
    c: Coincident(g9,g6)
    c: Horizontal(g6)
    c: Horizontal(g8)
    c: Vertical(g7)
    c: Vertical(g9)
    c: Equal(g2,g6)
    c: Equal(g5,g9)
    c: Vertical(g6,g4)
    c: DistanceX(g2,g2) = 13.7
    c: Vertical(g3)
    c: DistanceY(g3,g3) = 6.64
    c: DistanceY(g7,g3) = 25.25
    c: DistanceY(g-1,g10) = 70
    c: Vertical(g10,g1)
    c: DistanceY(g7,g10) = 16
    c: DistanceY(g1,g11) = 80
    c: Coincident(g12,g1)
    c: Coincident(g12,g11)
    c: Symmetric(g8,g7,g12)
    c: DistanceX(g12,g7) = 6.85
FEATURE [PartDesign::Pocket] Pocket019  label="trousUSB"
  BaseFeature = -> Pad024
  Direction = (0,0.707107,-0.707107)
  Length = 5
  Length2 = 5
  Profile = -> Sketch043
  ReferenceAxis = -> Sketch043 [N_Axis]
  Type = 1
FEATURE [Sketcher::SketchObject] Sketch044
  FullyConstrained = true
  MapMode = 5
  Placement = pos=(0,-93.2843,-2.84e-14) rot=(1,0,0;0.785398rad)
  Support = -> [DatumPlane011]
  expr: Constraints[0] = <<sp>>.distZeroPlanFAV
  expr: Constraints[10] = <<sp>>.switchTrouLong
  expr: Constraints[11] = <<sp>>.switchTrouLarg
  expr: Constraints[12] = <<sp>>.switchTrouLarg / 2
  expr: Constraints[1] = <<sp>>.largeurModuleBase / 2
  sketch-geometry (5):
    g0: GeomPoint X=-17.5 Y=20 Z=0
    g1: LineSegment StartX=-21.9 StartY=43.5 StartZ=0 EndX=-13.1 EndY=43.5 EndZ=0
    g2: LineSegment StartX=-13.1 StartY=43.5 StartZ=0 EndX=-13.1 EndY=29 EndZ=0
    g3: LineSegment StartX=-13.1 StartY=29 StartZ=0 EndX=-21.9 EndY=29 EndZ=0
    g4: LineSegment StartX=-21.9 StartY=29 StartZ=0 EndX=-21.9 EndY=43.5 EndZ=0
  constraints (14):
    c: DistanceY(g-1,g0) = 20
    c: DistanceX(g0,g-1) = 17.5
    c: Coincident(g1,g2)
    c: Coincident(g2,g3)
    c: Coincident(g3,g4)
    c: Coincident(g4,g1)
    c: Horizontal(g1)
    c: Horizontal(g3)
    c: Vertical(g2)
    c: Vertical(g4)
    c: DistanceY(g2,g2) = 14.5
    c: DistanceX(g1,g1) = 8.8
    c: DistanceX(g0,g2) = 4.4
    c: DistanceY(g0,g2) = 9
FEATURE [PartDesign::Pocket] Pocket020  label="trouSwitch"
  BaseFeature = -> Pocket019
  Direction = (0,0.707107,-0.707107)
  Length = 5
  Length2 = 5
  Profile = -> Sketch044
  ReferenceAxis = -> Sketch044 [N_Axis]
  Type = 1
FEATURE [Sketcher::SketchObject] Sketch045
  AttachmentOffset = pos=(0,0,-10) rot=(0,0,1;0rad)
  FullyConstrained = true
  MapMode = 5
  Placement = pos=(0,-86.2132,-7.07107) rot=(1,0,0;0.785398rad)
  Support = -> [DatumPlane011]
  expr: Constraints[1] = <<sp>>.largeurModuleBase / 2
  sketch-geometry (2):
    g0: GeomPoint X=-17.5 Y=70 Z=0
    g1: Circle CenterX=-17.5 CenterY=70 CenterZ=0 NormalX=0 NormalY=0 NormalZ=1 AngleXU=0 Radius=2
  constraints (4):
    c: DistanceY(g-1,g0) = 70
    c: DistanceX(g0,g-1) = 17.5
    c: Coincident(g1,g0)
    c: Diameter(g1) = 4
FEATURE [PartDesign::Pocket] Pocket021  label="trouPilone"
  BaseFeature = -> Pocket020
  Direction = (0,0.707107,-0.707107)
  Length = 5
  Length2 = 5
  Profile = -> Sketch045
  ReferenceAxis = -> Sketch045 [N_Axis]
  Type = 1
FEATURE [PartDesign::Body] Body002  label="faceAvant"
  BaseFeature = -> Slice_child1
  Group = -> [Clone001,Thickness001,DatumPlane007,Sketch016,Pad005,Sketch017,Pad006,Sketch018,Pocket010,DatumPlane011,Sketch030,Pad014,Pad015,Sketch031,Pad016,Sketch039,Pocket018,Sketch042,Pad024,Sketch043,Pocket019,Sketch044,Pocket020,Sketch045,Pocket021]
  Origin = -> Origin003
  Tip = -> Pocket021
COMPONENT P2 — recipe-attached ("USB1", modeled in this document).
Construction recipe (the document's own serialized feature program — sketch geometry with constraints, then the solid features built on it; lengths are millimeters unless a unit is written):

FEATURE [Sketcher::SketchObject] Sketch  label="profileDeBase"
  FullyConstrained = true
  MapMode = 5
  Placement = pos=(0,0,0) rot=(0.57735,0.57735,0.57735;2.0944rad)
  Support = -> [YZ_Plane001]
  expr: Constraints[10] = <<sp>>.petitRetour
  expr: Constraints[11] = <<sp>>.angleFacePetitRetour
  expr: Constraints[12] = <<sp>>.Face
  expr: Constraints[13] = <<sp>>.angleFaceRetourHaut
  expr: Constraints[8] = <<sp>>.Base
  expr: Constraints[9] = <<sp>>.anglePetitRetourBase
  sketch-geometry (5):
    g0: LineSegment StartX=0 StartY=0 StartZ=0 EndX=-65 EndY=0 EndZ=0
    g1: LineSegment StartX=-65 StartY=0 StartZ=0 EndX=-79.1421 EndY=14.1421 EndZ=0
    g2: LineSegment StartX=-79.1421 StartY=14.1421 StartZ=0 EndX=-22.5736 EndY=70.7107 EndZ=0
    g3: LineSegment StartX=-22.5736 StartY=70.7107 StartZ=0 EndX=0 EndY=48.1371 EndZ=0
    g4: LineSegment StartX=0 StartY=48.1371 StartZ=0 EndX=0 EndY=0 EndZ=0
  constraints (14):
    c: Coincident(g-1,g0)
    c: Horizontal(g0)
    c: Coincident(g0,g1)
    c: Coincident(g1,g2)
    c: Coincident(g2,g3)
    c: PointOnObject(g3,g-2)
    c: Coincident(g3,g4)
    c: Coincident(g4,g0)
    c: DistanceX(g0,g0) = 65
    c: Angle(g0,g1) = 2.35619
    c: Distance(g1) = 20
    c: Angle(g1,g2) = 1.5708
    c: Distance(g2) = 80
    c: Angle(g2,g3) = 1.5708
FEATURE [PartDesign::Pad] Pad
  AllowMultiFace = false
  Direction = (1,-2e-16,3e-16)
  Length = 35
  Length2 = 100
  Placement = pos=(0,0,0) rot=(0.57735,0.57735,0.57735;2.0944rad)
  Profile = -> Sketch
  Reversed = true
  Type = 0
  expr: Length = <<sp>>.largeurModuleBase
FEATURE [PartDesign::Plane] DatumPlane
  AttachmentOffset = pos=(71,0,0) rot=(0,-1,0;0.785398rad)
  Length = 98.6412
  MapMode = 5
  Placement = pos=(-1.18e-14,1.18e-14,71) rot=(0.678598,0.678598,0.281085;3.68962rad)
  ResizeMode = 0
  Support = -> [Pad]
  Width = 63.0813
FEATURE [PartDesign::Body] Body  label="Base"
  Group = -> [Sketch,Pad,DatumPlane]
  Origin = -> Origin001
  Tip = -> Pad
COMPONENT P3 — same part as P2; its construction recipe is shown at P2.
COMPONENT P4 — same part as P2; its construction recipe is shown at P2.
COMPONENT P5 — same part as P2; its construction recipe is shown at P2.
COMPONENT P6 — recipe-attached ("tigeLaiton001", modeled in this document).
Construction recipe (the document's own serialized feature program — sketch geometry with constraints, then the solid features built on it; lengths are millimeters unless a unit is written):

FEATURE [PartDesign::Plane] DatumPlane012  label="planBaseTige"
  AttachmentOffset = pos=(0,0,-5.18) rot=(0,0,1;0rad)
  Length = 60
  MapMode = 5
  Placement = pos=(-5.18,1.2e-15,-1.2e-15) rot=(0.57735,0.57735,0.57735;2.0944rad)
  ResizeMode = 0
  Support = -> [YZ_Plane012]
  Width = 60
  expr: .AttachmentOffset.Base.z = -<<tige>>.planBaseTigeposX
FEATURE [Sketcher::SketchObject] Sketch032  label="sk_tiges"
  FullyConstrained = true
  MapMode = 5
  Placement = pos=(-5.18,1.2e-15,-1.2e-15) rot=(0.57735,0.57735,0.57735;2.0944rad)
  Support = -> [DatumPlane012]
  expr: Constraints[0] = <<tige>>.tigeDiam
  expr: Constraints[1] = <<tige>>.tigePosY
  expr: Constraints[2] = <<tige>>.tigePosX
  sketch-geometry (1):
    g0: Circle CenterX=-14 CenterY=14.3 CenterZ=0 NormalX=0 NormalY=0 NormalZ=1 AngleXU=0 Radius=1.25
  constraints (3):
    c: Diameter(g0) = 2.5
    c: DistanceY(g-1,g0) = 14.3
    c: DistanceX(g0,g-1) = 14
FEATURE [PartDesign::Pad] Pad017  label="tigeBasse"
  AllowMultiFace = false
  Direction = (1,-1e-16,1e-16)
  Length = 18.62
  Length2 = 100
  Placement = pos=(-5.18,1e-15,-1e-15) rot=(0.57735,0.57735,0.57735;2.0944rad)
  Profile = -> Sketch032
  Reversed = true
  Type = 0
  expr: Length = <<tige>>.tigeLong
FEATURE [PartDesign::Body] Body007  label="tigeLaiton"
  Group = -> [DatumPlane012,Sketch032,Pad017]
  Origin = -> Origin016
  Tip = -> Pad017
FEATURE [PartDesign::Plane] DatumPlane013  label="planTige2"
  AttachmentOffset = pos=(0,0,-5.18) rot=(0,0,1;0rad)
  Length = 60
  MapMode = 5
  Placement = pos=(-5.18,1.2e-15,-1.2e-15) rot=(0.57735,0.57735,0.57735;2.0944rad)
  ResizeMode = 0
  Support = -> [YZ_Plane014]
  Width = 60
  expr: .AttachmentOffset.Base.z = -<<tige>>.planBaseTigeposX
FEATURE [Sketcher::SketchObject] Sketch033  label="sk_tige2"
  FullyConstrained = true
  MapMode = 5
  Placement = pos=(-5.18,1.2e-15,-1.2e-15) rot=(0.57735,0.57735,0.57735;2.0944rad)
  Support = -> [DatumPlane013]
  expr: Constraints[0] = <<tige>>.tigeDiam
  expr: Constraints[1] = <<tige>>.tigePosX
  expr: Constraints[2] = <<tige>>.tigePosY + <<tige>>.xtEcartBroches
  sketch-geometry (1):
    g0: Circle CenterX=-14 CenterY=21.86 CenterZ=0 NormalX=0 NormalY=0 NormalZ=1 AngleXU=0 Radius=1.25
  constraints (3):
    c: Diameter(g0) = 2.5
    c: DistanceX(g0,g-1) = 14
    c: DistanceY(g-1,g0) = 21.86
FEATURE [PartDesign::Pad] Pad018
  AllowMultiFace = false
  Direction = (1,-1e-16,1e-16)
  Length = 18.62
  Length2 = 100
  Placement = pos=(-5.18,1e-15,-1e-15) rot=(0.57735,0.57735,0.57735;2.0944rad)
  Profile = -> Sketch033
  Reversed = true
  Type = 0
  expr: Length = <<tige>>.tigeLong
FEATURE [PartDesign::Body] Body008  label="tige2"
  Group = -> [DatumPlane013,Sketch033,Pad018]
  Origin = -> Origin018
  Tip = -> Pad018
COMPONENT P7 — geometry summary ("xtVisInsertFix"; no construction recipe available for this part):
  bounding box: 20.2 x 17.7 x 16.6 mm
  tessellated surface: 23,850 triangles
  volume: 1306 mm^3 (22% of its bounding box)
COMPONENT P8 — geometry summary ("xtVisInertMob"; no construction recipe available for this part):
  bounding box: 20.5 x 17.8 x 16.5 mm
  tessellated surface: 35,150 triangles
  volume: 1060 mm^3 (18% of its bounding box)
COMPONENT P9 — recipe-attached ("visInsertFavFix", modeled in this document).
Construction recipe (the document's own serialized feature program — sketch geometry with constraints, then the solid features built on it; lengths are millimeters unless a unit is written):

FEATURE [Sketcher::SketchObject] Sketch034  label="Sketch"
  FullyConstrained = false
  MapMode = 5
  Support = -> [XY_Plane015]
  sketch-geometry (1):
    g0: Circle CenterX=0 CenterY=0 CenterZ=0 NormalX=0 NormalY=0 NormalZ=1 AngleXU=0 Radius=2.75
  constraints (2):
    c: Coincident(g0,g-1)
    c: Diameter(g0) = 5.5
FEATURE [PartDesign::Pad] Pad019  label="tete"
  AllowMultiFace = false
  Direction = (1,1,1)
  Length = 3
  Length2 = 100
  Profile = -> Sketch034
  Type = 0
FEATURE [Sketcher::SketchObject] Sketch001
  FullyConstrained = false
  MapMode = 5
  Placement = pos=(0,0,0) rot=(1,0,0;3.14159rad)
  Support = -> [Pad019]
  sketch-geometry (1):
    g0: Circle CenterX=0 CenterY=0 CenterZ=0 NormalX=0 NormalY=0 NormalZ=1 AngleXU=0 Radius=1.5
  constraints (2):
    c: Coincident(g0,g-1)
    c: Diameter(g0) = 3
FEATURE [PartDesign::Pad] Pad020  label="corps"
  AllowMultiFace = false
  BaseFeature = -> Pad019
  Direction = (1,1,1)
  Length = 6
  Length2 = 100
  Profile = -> Sketch001
  Type = 0
FEATURE [PartDesign::Plane] DatumPlane014
  AttachmentOffset = pos=(0,0,3) rot=(0,0,1;0rad)
  Length = 60
  MapMode = 5
  Placement = pos=(0,0,3) rot=(0,0,1;0rad)
  ResizeMode = 0
  Support = -> [XY_Plane015]
  Width = 60
FEATURE [Sketcher::SketchObject] Sketch035  label="Sketch002"
  FullyConstrained = false
  MapMode = 5
  Placement = pos=(0,0,3) rot=(0,0,1;0rad)
  Support = -> [DatumPlane014]
  sketch-geometry (7):
    g0: LineSegment StartX=0.721688 StartY=-1.25 StartZ=0 EndX=1.44338 EndY=1.0119e-12 EndZ=0
    g1: LineSegment StartX=1.44338 StartY=1.0119e-12 StartZ=0 EndX=0.721688 EndY=1.25 EndZ=0
    g2: LineSegment StartX=0.721688 StartY=1.25 StartZ=0 EndX=-0.721688 EndY=1.25 EndZ=0
    g3: LineSegment StartX=-0.721688 StartY=1.25 StartZ=0 EndX=-1.44338 EndY=8.689e-13 EndZ=0
    g4: LineSegment StartX=-1.44338 StartY=8.689e-13 StartZ=0 EndX=-0.721688 EndY=-1.25 EndZ=0
    g5: LineSegment StartX=-0.721688 StartY=-1.25 StartZ=0 EndX=0.721688 EndY=-1.25 EndZ=0
    g6: Circle CenterX=0 CenterY=0 CenterZ=0 NormalX=0 NormalY=0 NormalZ=1 AngleXU=0 Radius=1.44338
  constraints (16):
    c: Coincident(g0,g1)
    c: Coincident(g1,g2)
    c: Coincident(g2,g3)
    c: Coincident(g3,g4)
    c: Coincident(g4,g5)
    c: Coincident(g5,g0)
    c: Equal(g0, g1-g5) x5
    c: PointOnObject(g0,g6)
    c: PointOnObject(g1,g6)
    c: PointOnObject(g2,g6)
    c: PointOnObject(g3,g6)
    c: PointOnObject(g4,g6)
    c: PointOnObject(g5,g6)
    c: Coincident(g6,g-1)
    c: Horizontal(g2)
    c: DistanceY(g0,g1) = 2.5
FEATURE [PartDesign::Pocket] Pocket016  label="emprunte"
  AllowMultiFace = false
  BaseFeature = -> Pad020
  Direction = (1,1,1)
  Length = 4
  Length2 = 100
  Profile = -> Sketch035
  Type = 0
FEATURE [PartDesign::Body] Body009  label="visTHCM3x6_FAV001"
  Group = -> [Sketch034,Pad019,Sketch001,Pad020,DatumPlane014,Sketch035,Pocket016]
  Origin = -> Origin019
  Placement = pos=(-6.5,-61.8718,6.01041) rot=(1,0,0;3.92699rad)
  Tip = -> Pocket016
COMPONENT P10 — recipe-attached ("visInserFavMob", modeled in this document).
Construction recipe (the document's own serialized feature program — sketch geometry with constraints, then the solid features built on it; lengths are millimeters unless a unit is written):

FEATURE [Sketcher::SketchObject] Sketch036
  FullyConstrained = false
  MapMode = 5
  Support = -> [XY_Plane016]
  sketch-geometry (1):
    g0: Circle CenterX=0 CenterY=0 CenterZ=0 NormalX=0 NormalY=0 NormalZ=1 AngleXU=0 Radius=2.75
  constraints (2):
    c: Coincident(g0,g-1)
    c: Diameter(g0) = 5.5
FEATURE [PartDesign::Pad] Pad021  label="tete001"
  AllowMultiFace = false
  Direction = (1,1,1)
  Length = 3
  Length2 = 100
  Profile = -> Sketch036
  Type = 0
FEATURE [Sketcher::SketchObject] Sketch037
  FullyConstrained = false
  MapMode = 5
  Placement = pos=(0,0,0) rot=(1,0,0;3.14159rad)
  Support = -> [Pad021]
  sketch-geometry (1):
    g0: Circle CenterX=0 CenterY=0 CenterZ=0 NormalX=0 NormalY=0 NormalZ=1 AngleXU=0 Radius=1.5
  constraints (2):
    c: Coincident(g0,g-1)
    c: Diameter(g0) = 3
FEATURE [PartDesign::Pad] Pad022  label="corps001"
  AllowMultiFace = false
  BaseFeature = -> Pad021
  Direction = (1,1,1)
  Length = 6
  Length2 = 100
  Profile = -> Sketch037
  Type = 0
FEATURE [PartDesign::Plane] DatumPlane015
  AttachmentOffset = pos=(0,0,3) rot=(0,0,1;0rad)
  Length = 60
  MapMode = 5
  Placement = pos=(0,0,3) rot=(0,0,1;0rad)
  ResizeMode = 0
  Support = -> [XY_Plane016]
  Width = 60
FEATURE [Sketcher::SketchObject] Sketch038
  FullyConstrained = false
  MapMode = 5
  Placement = pos=(0,0,3) rot=(0,0,1;0rad)
  Support = -> [DatumPlane015]
  sketch-geometry (7):
    g0: LineSegment StartX=0.721688 StartY=-1.25 StartZ=0 EndX=1.44338 EndY=1.0119e-12 EndZ=0
    g1: LineSegment StartX=1.44338 StartY=1.0119e-12 StartZ=0 EndX=0.721688 EndY=1.25 EndZ=0
    g2: LineSegment StartX=0.721688 StartY=1.25 StartZ=0 EndX=-0.721688 EndY=1.25 EndZ=0
    g3: LineSegment StartX=-0.721688 StartY=1.25 StartZ=0 EndX=-1.44338 EndY=8.689e-13 EndZ=0
    g4: LineSegment StartX=-1.44338 StartY=8.689e-13 StartZ=0 EndX=-0.721688 EndY=-1.25 EndZ=0
    g5: LineSegment StartX=-0.721688 StartY=-1.25 StartZ=0 EndX=0.721688 EndY=-1.25 EndZ=0
    g6: Circle CenterX=0 CenterY=0 CenterZ=0 NormalX=0 NormalY=0 NormalZ=1 AngleXU=0 Radius=1.44338
  constraints (16):
    c: Coincident(g0,g1)
    c: Coincident(g1,g2)
    c: Coincident(g2,g3)
    c: Coincident(g3,g4)
    c: Coincident(g4,g5)
    c: Coincident(g5,g0)
    c: Equal(g0, g1-g5) x5
    c: PointOnObject(g0,g6)
    c: PointOnObject(g1,g6)
    c: PointOnObject(g2,g6)
    c: PointOnObject(g3,g6)
    c: PointOnObject(g4,g6)
    c: PointOnObject(g5,g6)
    c: Coincident(g6,g-1)
    c: Horizontal(g2)
    c: DistanceY(g0,g1) = 2.5
FEATURE [PartDesign::Pocket] Pocket017  label="emprunte001"
  AllowMultiFace = false
  BaseFeature = -> Pad022
  Direction = (1,1,1)
  Length = 4
  Length2 = 100
  Profile = -> Sketch038
  Type = 0
FEATURE [PartDesign::Body] Body010  label="visTHCM3x6_FAV002"
  Group = -> [Sketch036,Pad021,Sketch037,Pad022,DatumPlane015,Sketch038,Pocket017]
  Origin = -> Origin020
  Placement = pos=(-28.5,-61.8718,6.01041) rot=(1,0,0;3.92699rad)
  Tip = -> Pocket017
  expr: .Placement.Base.x = -(<<sp>>.largeurModuleBase - 6.5)
COMPONENT P11 — recipe-attached ("plaque", modeled in this document).
Construction recipe (the document's own serialized feature program — sketch geometry with constraints, then the solid features built on it; lengths are millimeters unless a unit is written):

FEATURE [Sketcher::SketchObject] Sketch040
  FullyConstrained = true
  MapMode = 5
  Support = -> [XY_Plane022]
  sketch-geometry (5):
    g0: LineSegment StartX=-11 StartY=18 StartZ=0 EndX=-11 EndY=-18 EndZ=0
    g1: LineSegment StartX=-11 StartY=-18 StartZ=0 EndX=11 EndY=-18 EndZ=0
    g2: LineSegment StartX=11 StartY=-18 StartZ=0 EndX=11 EndY=18 EndZ=0
    g3: LineSegment StartX=11 StartY=18 StartZ=0 EndX=-11 EndY=18 EndZ=0
    g4: GeomPoint X=0 Y=0 Z=0
  constraints (12):
    c: Coincident(g0,g1)
    c: Coincident(g1,g2)
    c: Coincident(g2,g3)
    c: Coincident(g3,g0)
    c: Horizontal(g1)
    c: Horizontal(g3)
    c: Vertical(g0)
    c: Vertical(g2)
    c: Symmetric(g1,g0,g4)
    c: Coincident(g4,g-1)
    c: DistanceY(g2,g2) = 36
    c: DistanceX(g3,g3) = 22
FEATURE [PartDesign::Pad] Pad023
  Direction = (0,0,1)
  Length = 1.6
  Length2 = 10
  Profile = -> Sketch040
  ReferenceAxis = -> Sketch040 [N_Axis]
  Type = 0
FEATURE [PartDesign::Body] Body011
  Group = -> [Sketch040,Pad023]
  Origin = -> Origin026
  Tip = -> Pad023
PROVENANCE & LICENSES
A FreeCAD (.FCStd) document from a public repository crawl; recipes are the document's own serialized feature recipes (and, for linked parts, companion documents' recipes).
License: as declared in the source repository (recorded in the dataset sidecar).
